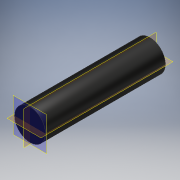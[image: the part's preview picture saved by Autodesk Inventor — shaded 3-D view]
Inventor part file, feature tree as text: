
AUTODESK INVENTOR PART (.ipt)
format: ipt  version: 2017 (Build 210142000, 142)  size: 110,080 bytes
history: native  units: mm
features: extrude x2, sketch x2
ambient origin geometry x8: Origin, YZ Plane, XZ Plane, XY Plane, X Axis, Y Axis, Z Axis, Center Point
bodies: Solid1 (feature_tree)
feature tree (4):
  extrude  "Extrusion1"  Depth=16.0mm
  extrude  "Extrusion2"  Depth=2.0mm
  sketch  "Sketch1"  dims[d1=18.0mm d3=16.0mm]
  sketch  "Sketch2"  dims[d4=70.0mm d5=0.0mm d6=1.0mm d7=16.0mm d8=2.0mm d9=0.0mm]
